# Revit family: IS_BuiltIn_A1000_BIM_DE
name_source: partatom
category: Plumbing Fixtures
revit_build: Autodesk Revit MEP 2016 (Build: 20161004_0715(x64)
units: mm (PartAtom-declared; Revit-internal decimal feet)

## family parameters
Cut with Voids When Loaded = No
Host = Face
OmniClass Number = 23.45.55.17
OmniClass Title = Mixing Faucets
Part Type = Normal
Room Calculation Point = No
Round Connector Dimension = Use Diameter
Shared = Yes

## types (1)
- A1000NU Built-In Bath Shower Mixer Kit1/Easy-Box
    Accessories = www.idealstandard.de/ersatzteile
    AreaUnits = millimeters
    Assembly Code = C1030200
    AssetType = Fixed
    BIMobject category = Taps & Mixers
    BREEAMApproved = No
    BarCode = 4015413321013
    Brand = Ideal Standard
    Brand url = http://www.idealstandard.de
    CWFU = 0
    Color = Chrome
    ConnectionType = Plumbing
    Cost = 0 $
    Default Elevation = 800 mm
    Description = Built-In Bath Shower Mixer Kit1/Easy-Box
    DurationUnit = year
    EAN code = https://4015413321013
    ECA = No
    Edition number = 1
    ExpectedLife = 30
    FaucetFunction = MIXED
    FaucetOperation = OTHER
    FaucetType = OTHER
    Features = BUILT-IN BTH SHR MXR KIT1/EASY-BOX
    Finish = Chrome
    HWFU = 0
    IfcExportAs = IfcValveType
    IfcExportType = FAUCET
    InstallationInstructions = www.idealstandard.de/produkte
    LinearUnits = millimeters
    Manufacturer name = Ideal Standard
    ManufacturerURL = www.idealstandard.de
    Material = Brass
    Material main = Brass
    Model = A1000NU
    ModelNumber = A1000NU
    ModelReference = Built-In Bath Shower Mixer Kit1/Easy-Box
    NBSReference = 45-35-70/???
    Name = BUILT-IN BTH SHR MXR KIT1/EASY-BOX
    NettWeight = 0.986 Kg
    Nominal height = 148 mm
    Nominal width = 148 mm
    NominalLength = 0 mm  [stored 0 ft]
    Product Guid = 589db18a-44e0-4533-b983-931844e90fb0
    Product SKU = A1000
    Product data url = https://bimobject.com
    Product family = EASY-BOX
    Product group = Built-in
    Product url = http://www.idealspec.co.uk
    ProductInformation = www.idealstandard.de/produkte
    QR code = http://bimobject.com
    Shape = Sculptured
    Size = 140 x 145 x 145 mm
    Space = Internal
    SpareParts = www.idealstandard.de/ersatzteile
    TMV3 = No
    Technical description = http://www.idealspec.co.uk
    TestPressure = 10 Bar
    URL = www.idealspec.co.uk
    Uniclass 2015 Code = Pr_40_20
    Uniclass 2015 Name = Sanitary fittings and accessories
    ValveMechanism = ceramic disc
    ValveOperation = lever
    Version = 1
    VolumeUnits = Litres
    WFU = 0
    WRAS = No
    WarrantyDescription = Manufacturers Warranty
    WarrantyDurationParts = 5
    WarrantyDurationUnit = year
    WaterEfficientProduct = No
    Weight Net (Kg) = 0.99
    WorkingPressure = 0.5-3 Bar

note: [stored X ft] marks values corroborated as IEEE doubles in the binary element streams (Revit-internal decimal feet)

## geometry (parser evidence)
native form markers: Sweep x3
no freeform markers — native parametric forms only
